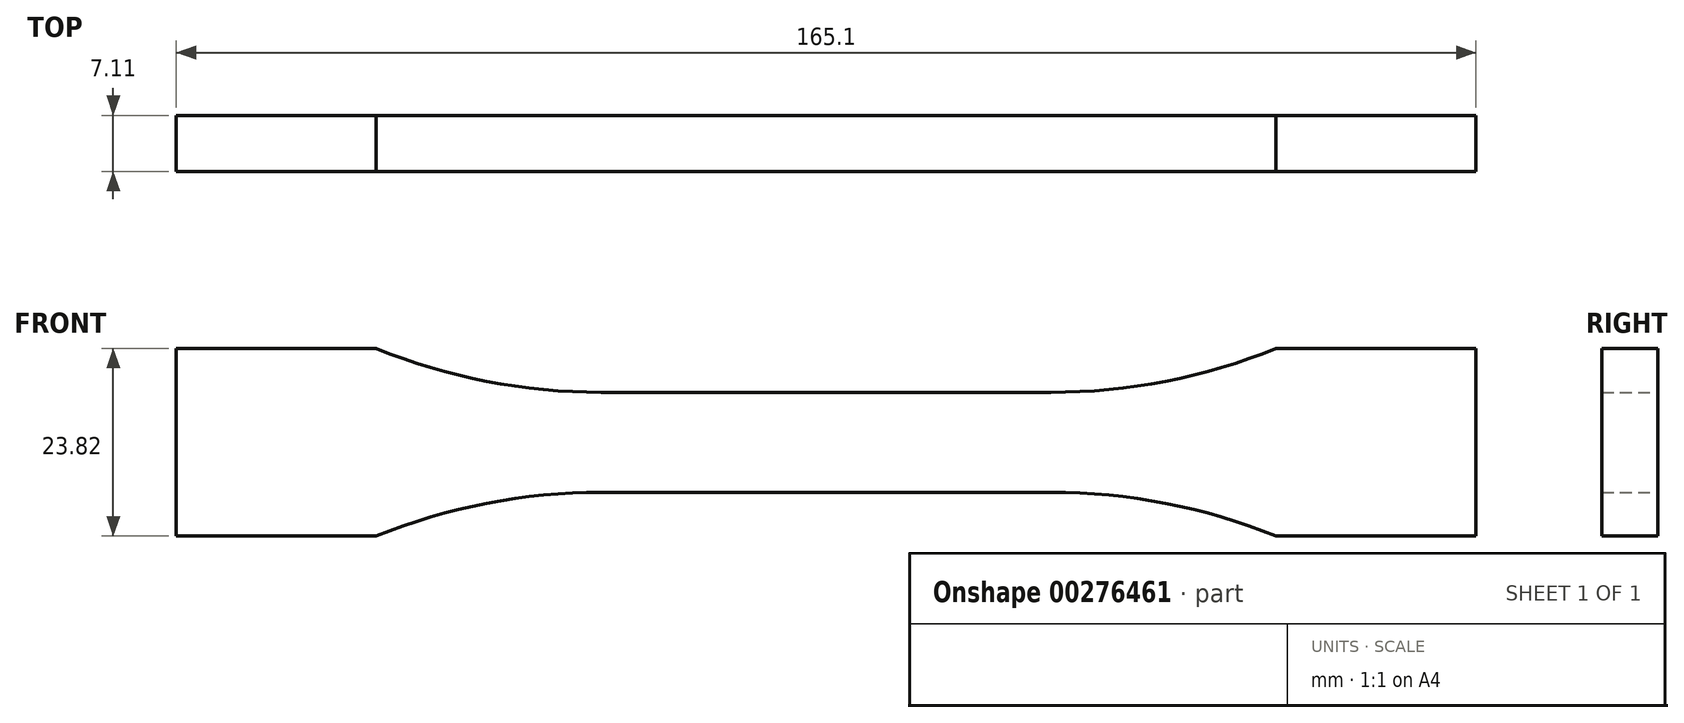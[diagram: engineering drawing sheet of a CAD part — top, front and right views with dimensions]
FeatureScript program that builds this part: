
annotation { "Feature Type Name" : "Feature", "Feature Type Description" : "" }
export const myFeature = defineFeature(function(context is Context, id is Id, definition is map)
    precondition{}
    {
        {
            var Q0;
            Q0=qCreatedBy(makeId("Front.planeOp"),FACE);
            var sketch = newSketch(context, id + "F0", { "sketchPlane" : qUnion([Q0])});
            skLineSegment(sketch, "E0", {"start": v(0, 6.35) * mm, "end": v(28.58, 6.35) * mm});
            skArc(sketch, "E1", {"start": v(28.58, 6.35) * mm, "mid": v(43.13, 7.75) * mm, "end": v(57.15, 11.91) * mm});
            skLineSegment(sketch, "E2", {"start": v(57.15, 11.91) * mm, "end": v(82.55, 11.91) * mm});
            skLineSegment(sketch, "E3.MirrorCS", {"start": v(57.15, -11.91) * mm, "end": v(82.55, -11.91) * mm});
            skLineSegment(sketch, "E4.MirrorCS", {"start": v(0, -6.35) * mm, "end": v(28.58, -6.35) * mm});
            skArc(sketch, "E5.MirrorCS", {"start": v(28.58, -6.35) * mm, "mid": v(43.13, -7.75) * mm, "end": v(57.15, -11.91) * mm});
            skLineSegment(sketch, "E6.MirrorCS", {"start": v(0, 6.35) * mm, "end": v(-28.58, 6.35) * mm});
            skArc(sketch, "E7.MirrorCS", {"start": v(-28.58, 6.35) * mm, "mid": v(-43.13, 7.75) * mm, "end": v(-57.15, 11.91) * mm});
            skLineSegment(sketch, "E8.MirrorCS", {"start": v(-57.15, 11.91) * mm, "end": v(-82.55, 11.91) * mm});
            skLineSegment(sketch, "E9.MirrorCS", {"start": v(-57.15, -11.91) * mm, "end": v(-82.55, -11.91) * mm});
            skLineSegment(sketch, "E10.MirrorCS", {"start": v(0, -6.35) * mm, "end": v(-28.58, -6.35) * mm});
            skArc(sketch, "E11.MirrorCS", {"start": v(-28.58, -6.35) * mm, "mid": v(-43.13, -7.75) * mm, "end": v(-57.15, -11.91) * mm});
            skLineSegment(sketch, "E12", {"start": v(-82.55, 11.91) * mm, "end": v(-82.55, -11.91) * mm});
            skLineSegment(sketch, "E13", {"start": v(82.55, 11.91) * mm, "end": v(82.55, -11.91) * mm});
            skSolve(sketch);
        }
        {
            var Q0;
            Q0 = qSketchRegion(id + "F0", true);
            extrude(context, id + "F1", {"entities" : qUnion([Q0]), "depth" : 7.11 * mm});
        }
    });
